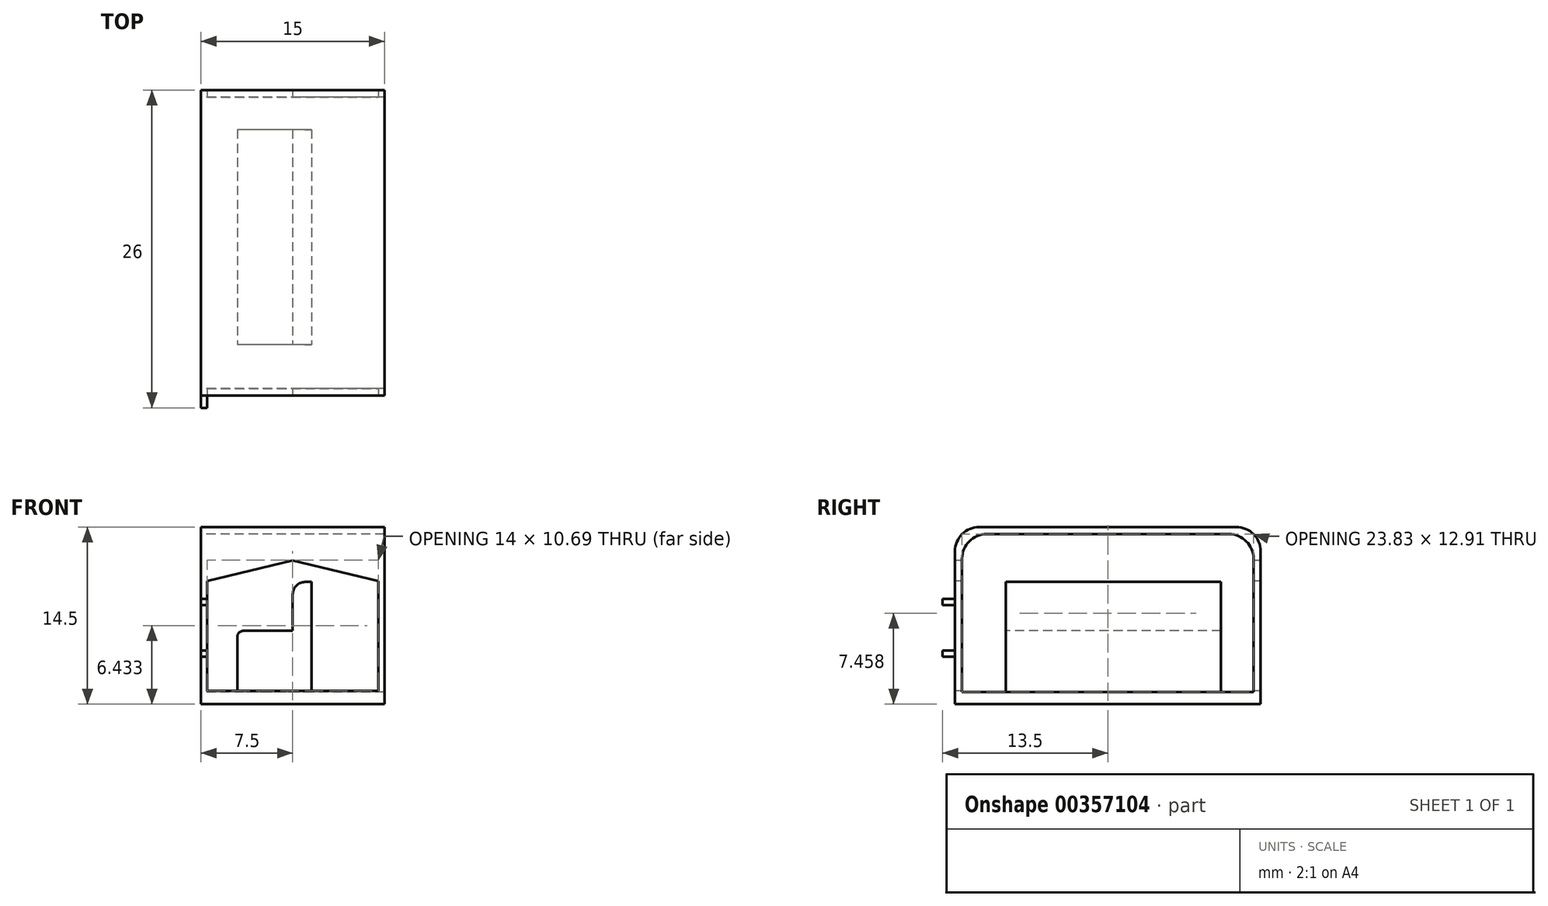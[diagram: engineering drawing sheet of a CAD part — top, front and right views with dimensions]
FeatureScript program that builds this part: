
annotation { "Feature Type Name" : "Feature", "Feature Type Description" : "" }
export const myFeature = defineFeature(function(context is Context, id is Id, definition is map)
    precondition{}
    {
        {
            var Q0;
            Q0=qCreatedBy(makeId("Top.planeOp"),FACE);
            var sketch = newSketch(context, id + "F0", { "sketchPlane" : qUnion([Q0])});
            skLineSegment(sketch, "E0.bottom", {"start": v(7.5, 12.5) * mm, "end": v(-7.5, 12.5) * mm});
            skLineSegment(sketch, "E0.top", {"start": v(7.5, -12.5) * mm, "end": v(-7.5, -12.5) * mm});
            skLineSegment(sketch, "E0.left", {"start": v(7.5, 12.5) * mm, "end": v(7.5, -12.5) * mm});
            skLineSegment(sketch, "E0.right", {"start": v(-7.5, 12.5) * mm, "end": v(-7.5, -12.5) * mm});
            skPoint(sketch, "E0.middle", {"position": v(0, 0) * mm});
            skSolve(sketch);
        }
        {
            var Q0;
            Q0 = qSketchRegion(id + "F0", true);
            extrude(context, id + "F1", {"entities" : qUnion([Q0]), "depth" : 14.5 * mm});
        }
        {
            var Q0;
            Q0=makeQuery(id+"F1.opExtrude","CAP_EDGE",EDGE,{"disambiguationData":[OSD([sQuery(id+"F0.wireOp",EDGE,"E0.bottom")])],"isStart":false});
            var Q1;
            Q1=makeQuery(id+"F1.opExtrude","CAP_EDGE",EDGE,{"disambiguationData":[OSD([sQuery(id+"F0.wireOp",EDGE,"E0.top")])],"isStart":false});
            fillet(context, id + "F2", {"entities" : qUnion([Q0, Q1]), "radius" : 2 * mm, "tangentPropagation" : true, "allowEdgeOverflow" : false});
        }
        {
            var Q0;
            Q0=makeQuery(id+"F1.opExtrude","SWEPT_FACE",FACE,{"disambiguationData":[OSD([sQuery(id+"F0.wireOp",EDGE,"E0.right")])]});
            var sketch = newSketch(context, id + "F3", { "sketchPlane" : qUnion([Q0])});
            skLineSegment(sketch, "E1.bottom", {"start": v(-11.91, 1) * mm, "end": v(11.91, 1) * mm});
            skLineSegment(sketch, "E1.top", {"start": v(-9.91, 13.91) * mm, "end": v(9.91, 13.91) * mm});
            skLineSegment(sketch, "E1.left", {"start": v(-11.91, 1) * mm, "end": v(-11.91, 11.91) * mm});
            skLineSegment(sketch, "E1.right", {"start": v(11.91, 1) * mm, "end": v(11.91, 11.91) * mm});
            skPoint(sketch, "E2.visualSharp", {"position": v(-11.91, 13.91) * mm});
            skArc(sketch, "E2.filletArc", {"start": v(-9.91, 13.91) * mm, "mid": v(-11.33, 13.33) * mm, "end": v(-11.91, 11.91) * mm});
            skPoint(sketch, "E3.visualSharp", {"position": v(11.91, 13.91) * mm});
            skArc(sketch, "E3.filletArc", {"start": v(11.91, 11.91) * mm, "mid": v(11.33, 13.33) * mm, "end": v(9.91, 13.91) * mm});
            skSolve(sketch);
        }
        {
            var Q0;
            Q0 = qSketchRegion(id + "F3", true);
            extrude(context, id + "F4", {"entities" : qUnion([Q0]), "operationType" : NewBodyOperationType.REMOVE, "oppositeDirection" : true, "depth" : 25 * mm});
        }
        {
            var Q0;
            Q0=makeQuery(id+"F1.opExtrude","SWEPT_FACE",FACE,{"disambiguationData":[OSD([sQuery(id+"F0.wireOp",EDGE,"E0.top")])]});
            var sketch = newSketch(context, id + "F5", { "sketchPlane" : qUnion([Q0])});
            skPoint(sketch, "E4.start.orphan", {"position": v(0, 0) * mm});
            skLineSegment(sketch, "E5", {"start": v(7, 10.1) * mm, "end": v(0, 11.78) * mm});
            skLineSegment(sketch, "E6", {"start": v(-7, 10.1) * mm, "end": v(0, 11.78) * mm});
            skPoint(sketch, "E7.orphan", {"position": v(6.87, 0) * mm});
            skPoint(sketch, "E8.end.orphan", {"position": v(-6.87, 0) * mm});
            skLineSegment(sketch, "E9", {"start": v(-7, 10.1) * mm, "end": v(-7, 1.1) * mm});
            skLineSegment(sketch, "E10", {"start": v(7, 10.1) * mm, "end": v(7, 1.1) * mm});
            skLineSegment(sketch, "E11", {"start": v(-7, 1.1) * mm, "end": v(7, 1.1) * mm});
            skLineSegment(sketch, "E12", {"start": v(7, 1.1) * mm, "end": v(7, 1.1) * mm});
            skSolve(sketch);
        }
        {
            var Q0;
            Q0 = qSketchRegion(id + "F5", true);
            extrude(context, id + "F6", {"entities" : qUnion([Q0]), "operationType" : NewBodyOperationType.REMOVE, "oppositeDirection" : true, "depth" : 25 * mm});
        }
        {
            var Q0;
            Q0=makeQuery(id+"F5.imprint","IMPRINT",FACE,{"disambiguationData":[TD([[makeQuery(id+"F5.imprint","IMPRINT",EDGE,{"derivedFrom":sQuery(id+"F5.wireOp",EDGE,"E5")}),-1.0]])]});
            var sketch = newSketch(context, id + "F7", { "sketchPlane" : qUnion([Q0])});
            skLineSegment(sketch, "E13.bottom", {"start": v(-7.5, 8.61) * mm, "end": v(-7, 8.61) * mm});
            skLineSegment(sketch, "E13.top", {"start": v(-7.5, 8.11) * mm, "end": v(-7, 8.11) * mm});
            skLineSegment(sketch, "E13.left", {"start": v(-7.5, 8.61) * mm, "end": v(-7.5, 8.11) * mm});
            skLineSegment(sketch, "E13.right", {"start": v(-7, 8.61) * mm, "end": v(-7, 8.11) * mm});
            skLineSegment(sketch, "E14.bottom", {"start": v(-7.5, 4.39) * mm, "end": v(-7, 4.39) * mm});
            skLineSegment(sketch, "E14.top", {"start": v(-7.5, 3.89) * mm, "end": v(-7, 3.89) * mm});
            skLineSegment(sketch, "E14.left", {"start": v(-7.5, 4.39) * mm, "end": v(-7.5, 3.89) * mm});
            skLineSegment(sketch, "E14.right", {"start": v(-7, 4.39) * mm, "end": v(-7, 3.89) * mm});
            skSolve(sketch);
        }
        {
            var Q0;
            Q0 = qSketchRegion(id + "F7", true);
            extrude(context, id + "F8", {"entities" : qUnion([Q0]), "operationType" : NewBodyOperationType.ADD, "depth" : 1 * mm});
        }
        {
            var Q0;
            Q0=makeQuery(id+"F4.boolean.opBoolean","COPY",FACE,{"derivedFrom":makeQuery(id+"F4.opExtrude","SWEPT_FACE",FACE,{"disambiguationData":[OSD([sQuery(id+"F3.wireOp",EDGE,"E1.bottom")])]})});
            var sketch = newSketch(context, id + "F9", { "sketchPlane" : qUnion([Q0])});
            skLineSegment(sketch, "E15.bottom", {"start": v(0, 9.26) * mm, "end": v(-4.53, 9.26) * mm});
            skLineSegment(sketch, "E15.top", {"start": v(0, -8.35) * mm, "end": v(-4.53, -8.35) * mm});
            skLineSegment(sketch, "E15.left", {"start": v(0, 9.26) * mm, "end": v(0, -8.35) * mm});
            skLineSegment(sketch, "E15.right", {"start": v(-4.53, 9.26) * mm, "end": v(-4.53, -8.35) * mm});
            skLineSegment(sketch, "E16.bottom", {"start": v(0, 9.26) * mm, "end": v(1.55, 9.26) * mm});
            skLineSegment(sketch, "E16.top", {"start": v(0, -8.35) * mm, "end": v(1.55, -8.35) * mm});
            skLineSegment(sketch, "E16.right", {"start": v(1.55, 9.26) * mm, "end": v(1.55, -8.35) * mm});
            skSolve(sketch);
        }
        {
            var Q0;
            {var subQ0=sQuery(id+"F9.wireOp",EDGE,"E15.bottom");Q0=makeQuery(id+"F9.imprint","IMPRINT",FACE,{"disambiguationData":[TD([[makeQuery(id+"F9.imprint","IMPRINT",EDGE,{"derivedFrom":subQ0}),1.0]])]});}
            extrude(context, id + "F10", {"entities" : qUnion([Q0]), "operationType" : NewBodyOperationType.ADD, "depth" : 5 * mm});
        }
        {
            var Q0;
            {var subQ3=sQuery(id+"F9.wireOp",EDGE,"E16.bottom");Q0=makeQuery(id+"F9.imprint","IMPRINT",FACE,{"disambiguationData":[TD([[makeQuery(id+"F9.imprint","IMPRINT",EDGE,{"derivedFrom":subQ3}),-1.0]])]});}
            extrude(context, id + "F11", {"entities" : qUnion([Q0]), "operationType" : NewBodyOperationType.ADD, "depth" : 9 * mm});
        }
        {
            var Q0;
            Q0=makeQuery(id+"F10.opExtrude","CAP_EDGE",EDGE,{"disambiguationData":[OSD([sQuery(id+"F9.wireOp",EDGE,"E15.right")])],"isStart":false});
            fillet(context, id + "F12", {"entities" : qUnion([Q0]), "radius" : .5 * mm, "tangentPropagation" : true, "allowEdgeOverflow" : false});
        }
        {
            var Q0;
            Q0=makeQuery(id+"F11.opExtrude","CAP_EDGE",EDGE,{"disambiguationData":[OSD([sQuery(id+"F9.wireOp",EDGE,"E15.left")])],"isStart":false});
            fillet(context, id + "F13", {"entities" : qUnion([Q0]), "radius" : 1 * mm, "tangentPropagation" : true, "allowEdgeOverflow" : false});
        }
    });
